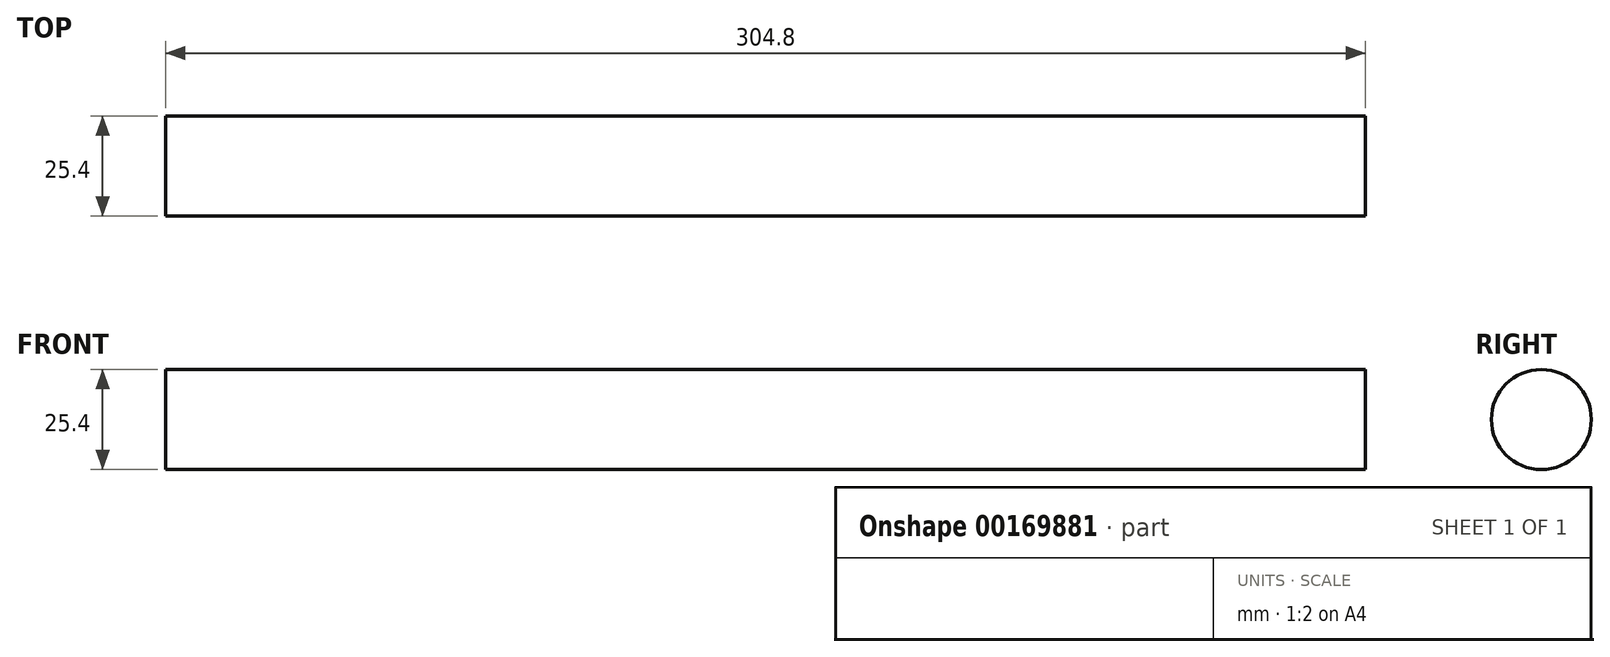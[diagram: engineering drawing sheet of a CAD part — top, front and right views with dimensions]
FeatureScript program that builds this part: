
annotation { "Feature Type Name" : "Feature", "Feature Type Description" : "" }
export const myFeature = defineFeature(function(context is Context, id is Id, definition is map)
    precondition{}
    {
        {
            var Q0;
            Q0=qCreatedBy(makeId("Right.planeOp"),FACE);
            var sketch = newSketch(context, id + "F0", { "sketchPlane" : qUnion([Q0])});
            skCircle(sketch, "E0", {"center": v(0, 0) * mm, "radius": 12.7 * mm});
            skSolve(sketch);
        }
        {
            var Q0;
            Q0 = qSketchRegion(id + "F0", true);
            extrude(context, id + "F1", {"entities" : qUnion([Q0]), "depth" : 304.8 * mm});
        }
    });
